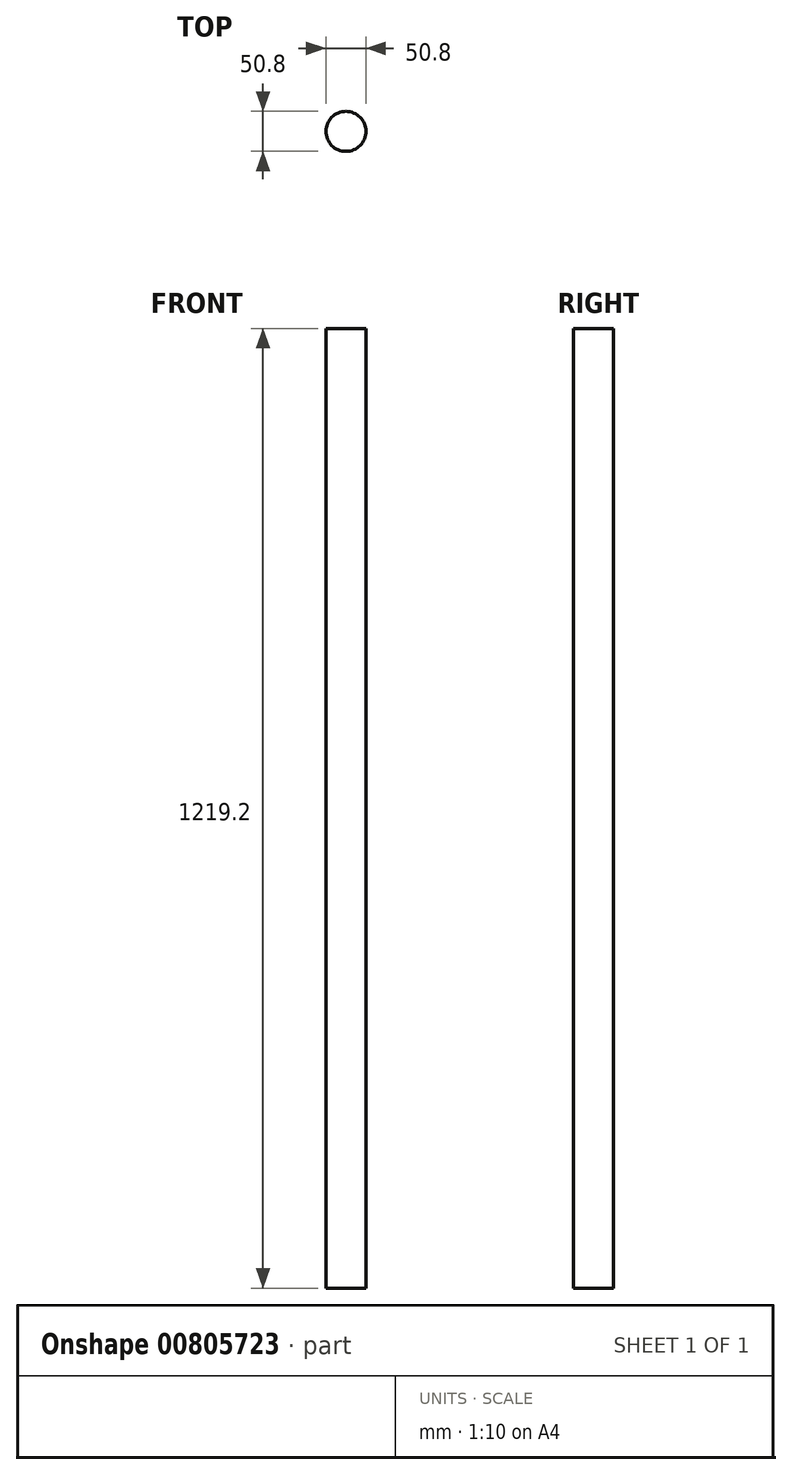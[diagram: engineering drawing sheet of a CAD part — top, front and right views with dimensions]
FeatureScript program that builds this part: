
annotation { "Feature Type Name" : "Feature", "Feature Type Description" : "" }
export const myFeature = defineFeature(function(context is Context, id is Id, definition is map)
    precondition{}
    {
        {
            var Q0;
            Q0=qCreatedBy(makeId("Top.planeOp"),FACE);
            var sketch = newSketch(context, id + "F0", { "sketchPlane" : qUnion([Q0])});
            skCircle(sketch, "E0", {"center": v(0, 0) * mm, "radius": 25.4 * mm});
            skSolve(sketch);
        }
        {
            var Q0;
            Q0 = qSketchRegion(id + "F0", true);
            extrude(context, id + "F1", {"entities" : qUnion([Q0]), "depth" : 1219.2 * mm, "offsetDistance" : 25.4 * mm, "symmetric" : true});
        }
    });
